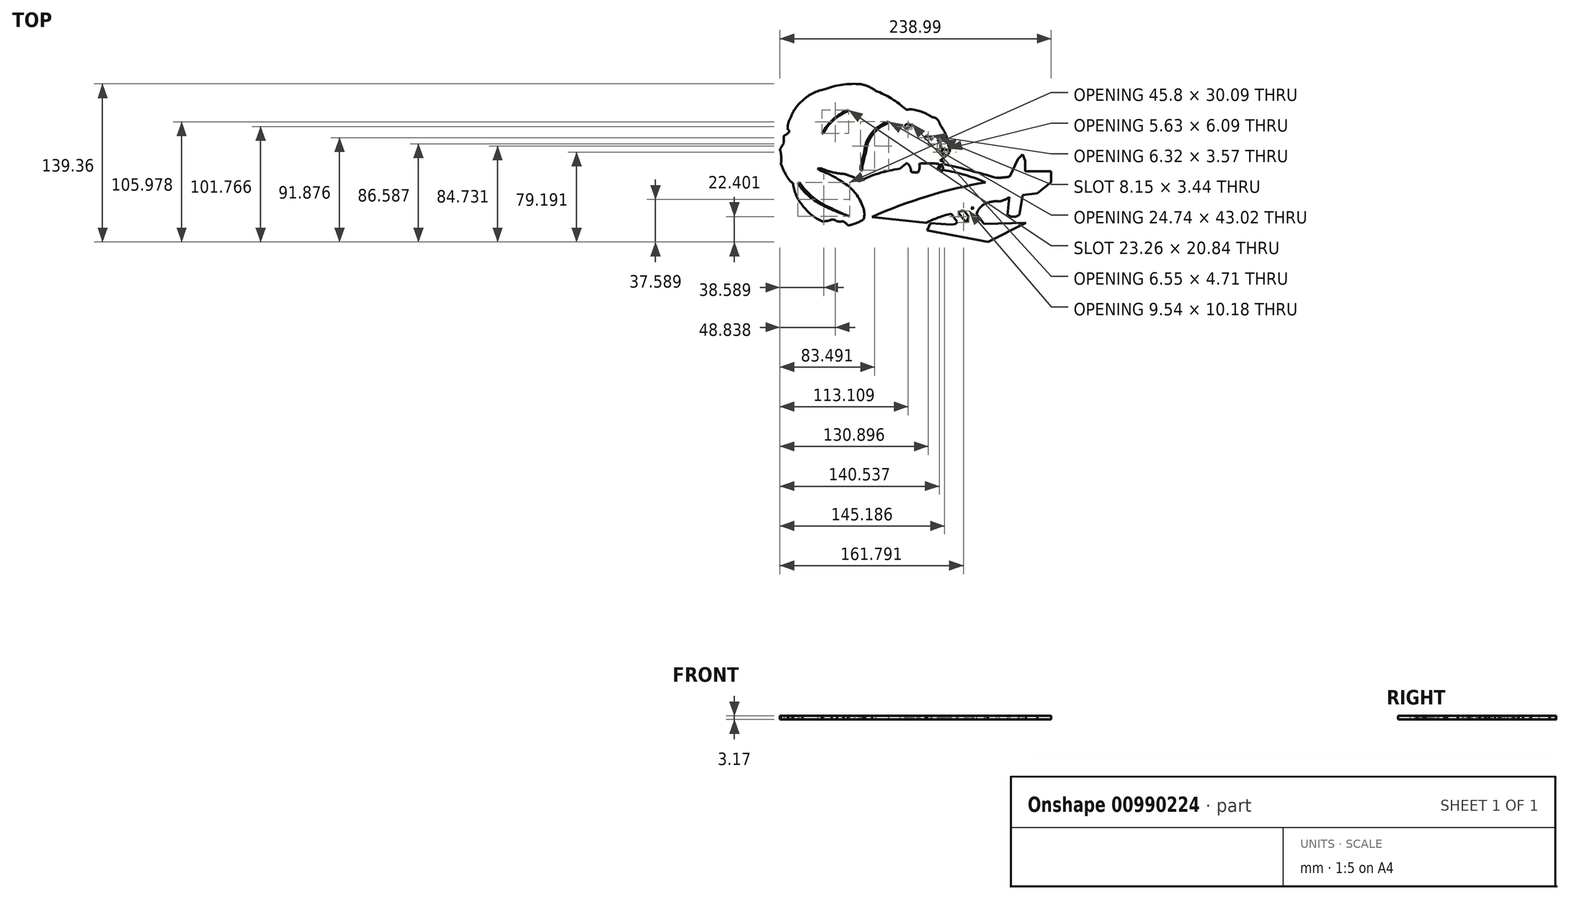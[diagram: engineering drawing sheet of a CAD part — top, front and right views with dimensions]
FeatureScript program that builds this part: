
annotation { "Feature Type Name" : "Feature", "Feature Type Description" : "" }
export const myFeature = defineFeature(function(context is Context, id is Id, definition is map)
    precondition{}
    {
        {
            var Q0;
            Q0=qCreatedBy(makeId("Top.planeOp"),FACE);
            var sketch = newSketch(context, id + "F0", { "sketchPlane" : qUnion([Q0])});
            skArc(sketch, "E0", {"start": v(160.46, 90.83) * mm, "mid": v(162.98, 93) * mm, "end": v(164.83, 95.76) * mm});
            skArc(sketch, "E1", {"start": v(164.83, 95.76) * mm, "mid": v(164.52, 98.7) * mm, "end": v(163, 101.22) * mm});
            skArc(sketch, "E2", {"start": v(163, 101.22) * mm, "mid": v(163.59, 103.27) * mm, "end": v(163, 105.33) * mm});
            skArc(sketch, "E3", {"start": v(163, 105.33) * mm, "mid": v(160.72, 111.62) * mm, "end": v(157.27, 117.36) * mm});
            skArc(sketch, "E4", {"start": v(155.17, 121.91) * mm, "mid": v(156.06, 119.56) * mm, "end": v(157.27, 117.36) * mm});
            skArc(sketch, "E5", {"start": v(155.17, 121.91) * mm, "mid": v(152.64, 124.68) * mm, "end": v(149.06, 125.83) * mm});
            skArc(sketch, "E6", {"start": v(149.06, 125.83) * mm, "mid": v(139.42, 130.68) * mm, "end": v(128.83, 132.76) * mm});
            skArc(sketch, "E7", {"start": v(126, 132.76) * mm, "mid": v(127.42, 132.3) * mm, "end": v(128.83, 132.76) * mm});
            skArc(sketch, "E8", {"start": v(126, 132.76) * mm, "mid": v(113.45, 142.03) * mm, "end": v(99.47, 148.97) * mm});
            skArc(sketch, "E9", {"start": v(99.47, 148.97) * mm, "mid": v(93.3, 152.63) * mm, "end": v(86.46, 154.73) * mm});
            skArc(sketch, "E10", {"start": v(86.46, 154.73) * mm, "mid": v(69.87, 154.35) * mm, "end": v(53.83, 150.08) * mm});
            skArc(sketch, "E11", {"start": v(53.83, 150.08) * mm, "mid": v(43.24, 146.4) * mm, "end": v(34.23, 139.7) * mm});
            skArc(sketch, "E12", {"start": v(34.23, 139.7) * mm, "mid": v(28.64, 133.35) * mm, "end": v(24.76, 125.83) * mm});
            skArc(sketch, "E13", {"start": v(24.76, 125.83) * mm, "mid": v(22.51, 120.68) * mm, "end": v(21.86, 115.1) * mm});
            skArc(sketch, "E14", {"start": v(23.32, 112.91) * mm, "mid": v(22.86, 114.18) * mm, "end": v(21.86, 115.1) * mm});
            skArc(sketch, "E15", {"start": v(18.67, 109.45) * mm, "mid": v(21.21, 110.9) * mm, "end": v(23.32, 112.91) * mm});
            skArc(sketch, "E16", {"start": v(18.67, 109.45) * mm, "mid": v(18.36, 106.3) * mm, "end": v(18.67, 103.16) * mm});
            skArc(sketch, "E17", {"start": v(18.67, 103.16) * mm, "mid": v(16.8, 100.19) * mm, "end": v(15.01, 97.17) * mm});
            skArc(sketch, "E18", {"start": v(16.05, 93.03) * mm, "mid": v(15.68, 95.14) * mm, "end": v(15.01, 97.17) * mm});
            skArc(sketch, "E19", {"start": v(16.05, 84.77) * mm, "mid": v(16.17, 88.9) * mm, "end": v(16.05, 93.03) * mm});
            skArc(sketch, "E20", {"start": v(16.05, 84.77) * mm, "mid": v(18.51, 78.47) * mm, "end": v(21.86, 72.6) * mm});
            skArc(sketch, "E21", {"start": v(21.86, 72.6) * mm, "mid": v(23.94, 69.68) * mm, "end": v(26.73, 67.43) * mm});
            skArc(sketch, "E22", {"start": v(26.73, 67.43) * mm, "mid": v(29.3, 56.97) * mm, "end": v(35.1, 47.9) * mm});
            skArc(sketch, "E23", {"start": v(35.1, 47.9) * mm, "mid": v(42.8, 39.74) * mm, "end": v(52.45, 34) * mm});
            skArc(sketch, "E24", {"start": v(74.96, 30.33) * mm, "mid": v(82.12, 32.25) * mm, "end": v(88.74, 35.62) * mm});
            skArc(sketch, "E25", {"start": v(88.74, 35.62) * mm, "mid": v(89.4, 41.86) * mm, "end": v(87.7, 47.9) * mm});
            skArc(sketch, "E26", {"start": v(87.7, 47.9) * mm, "mid": v(80.74, 59.73) * mm, "end": v(70.25, 68.58) * mm});
            skArc(sketch, "E27", {"start": v(70.25, 68.58) * mm, "mid": v(60.84, 74.2) * mm, "end": v(50.84, 78.68) * mm});
            skArc(sketch, "E28", {"start": v(48.2, 80.6) * mm, "mid": v(49.41, 79.49) * mm, "end": v(50.84, 78.68) * mm});
            skArc(sketch, "E29", {"start": v(53.83, 79.6) * mm, "mid": v(51.1, 80.62) * mm, "end": v(48.2, 80.6) * mm});
            skArc(sketch, "E30", {"start": v(53.83, 79.6) * mm, "mid": v(62.89, 76.93) * mm, "end": v(72.24, 75.62) * mm});
            skArc(sketch, "E31", {"start": v(72.24, 75.62) * mm, "mid": v(76.5, 74.1) * mm, "end": v(80.77, 72.6) * mm});
            skArc(sketch, "E32", {"start": v(126, 84.77) * mm, "mid": v(102.6, 81.62) * mm, "end": v(80.77, 72.6) * mm});
            skArc(sketch, "E33", {"start": v(153.6, 84.77) * mm, "mid": v(145.69, 85.05) * mm, "end": v(137.76, 84.77) * mm});
            skArc(sketch, "E34", {"start": v(156.02, 87.46) * mm, "mid": v(158.32, 89.04) * mm, "end": v(160.46, 90.83) * mm});
            skArc(sketch, "E35", {"start": v(160.46, 84.77) * mm, "mid": v(158.62, 86.74) * mm, "end": v(156.02, 87.46) * mm});
            skArc(sketch, "E36", {"start": v(157.83, 95.76) * mm, "mid": v(158.13, 93.86) * mm, "end": v(159.04, 92.17) * mm});
            skArc(sketch, "E37", {"start": v(161.22, 97.17) * mm, "mid": v(159.2, 97.25) * mm, "end": v(157.83, 95.76) * mm});
            skArc(sketch, "E38", {"start": v(161.22, 97.17) * mm, "mid": v(162.11, 96.82) * mm, "end": v(163, 97.17) * mm});
            skArc(sketch, "E39", {"start": v(157.27, 98.2) * mm, "mid": v(156.43, 102.55) * mm, "end": v(154.16, 106.35) * mm});
            skArc(sketch, "E40", {"start": v(131.4, 118.08) * mm, "mid": v(128.77, 116.93) * mm, "end": v(126.57, 115.1) * mm});
            skArc(sketch, "E41", {"start": v(124.85, 116.87) * mm, "mid": v(125.44, 115.73) * mm, "end": v(126.57, 115.1) * mm});
            skArc(sketch, "E42", {"start": v(128.8, 119.69) * mm, "mid": v(126.14, 119.25) * mm, "end": v(124.85, 116.87) * mm});
            skArc(sketch, "E43", {"start": v(131.4, 118.08) * mm, "mid": v(130.22, 119.08) * mm, "end": v(128.8, 119.69) * mm});
            skArc(sketch, "E44", {"start": v(149.06, 105.83) * mm, "mid": v(147.66, 108.15) * mm, "end": v(145.22, 109.33) * mm});
            skArc(sketch, "E45", {"start": v(145.22, 109.33) * mm, "mid": v(143.62, 108.94) * mm, "end": v(142.75, 107.55) * mm});
            skArc(sketch, "E46", {"start": v(110.87, 120.48) * mm, "mid": v(96.75, 110.42) * mm, "end": v(90.85, 94.1) * mm});
            skArc(sketch, "E47", {"start": v(90.85, 94.1) * mm, "mid": v(89.5, 90.08) * mm, "end": v(88.7, 85.92) * mm});
            skArc(sketch, "E48", {"start": v(75.48, 131.3) * mm, "mid": v(62.46, 123.3) * mm, "end": v(53.05, 111.25) * mm});
            skArc(sketch, "E49", {"start": v(88.7, 85.92) * mm, "mid": v(87.74, 82.48) * mm, "end": v(87.85, 78.91) * mm});
            skArc(sketch, "E50", {"start": v(120.78, 80.26) * mm, "mid": v(102.14, 76.26) * mm, "end": v(84.5, 69.05) * mm});
            skArc(sketch, "E51", {"start": v(130.6, 77.85) * mm, "mid": v(129.87, 81.62) * mm, "end": v(127.68, 84.77) * mm});
            skArc(sketch, "E52", {"start": v(133.15, 77.4) * mm, "mid": v(132.91, 80.68) * mm, "end": v(132.6, 83.96) * mm});
            skArc(sketch, "E53", {"start": v(135.6, 77.21) * mm, "mid": v(135.81, 79.9) * mm, "end": v(135.88, 82.59) * mm});
            skArc(sketch, "E54", {"start": v(136.8, 77.21) * mm, "mid": v(138.13, 80.88) * mm, "end": v(137.76, 84.77) * mm});
            skArc(sketch, "E55", {"start": v(153.6, 80.22) * mm, "mid": v(155.03, 82.27) * mm, "end": v(154.93, 84.77) * mm});
            skArc(sketch, "E56", {"start": v(154.84, 79.58) * mm, "mid": v(156.54, 81.91) * mm, "end": v(156.94, 84.77) * mm});
            skArc(sketch, "E57", {"start": v(158.49, 79.49) * mm, "mid": v(158.5, 82.36) * mm, "end": v(156.94, 84.77) * mm});
            skArc(sketch, "E58", {"start": v(156.94, 78.78) * mm, "mid": v(157.72, 79.11) * mm, "end": v(158.49, 79.49) * mm});
            skArc(sketch, "E59", {"start": v(157.68, 77.98) * mm, "mid": v(159.94, 80.65) * mm, "end": v(160.28, 84.13) * mm});
            skArc(sketch, "E60", {"start": v(160.28, 84.13) * mm, "mid": v(159.87, 85.19) * mm, "end": v(159.35, 86.2) * mm});
            skArc(sketch, "E61", {"start": v(153.6, 80.22) * mm, "mid": v(154.06, 79.6) * mm, "end": v(154.84, 79.58) * mm});
            skArc(sketch, "E62", {"start": v(135.6, 77.21) * mm, "mid": v(136.2, 76.97) * mm, "end": v(136.8, 77.21) * mm});
            skArc(sketch, "E63", {"start": v(133.15, 77.4) * mm, "mid": v(134.35, 76.94) * mm, "end": v(135.6, 77.21) * mm});
            skArc(sketch, "E64", {"start": v(130.6, 77.85) * mm, "mid": v(131.8, 77.22) * mm, "end": v(133.15, 77.4) * mm});
            skArc(sketch, "E65", {"start": v(151.46, 80.22) * mm, "mid": v(145.6, 80.37) * mm, "end": v(139.74, 80.36) * mm});
            skArc(sketch, "E66", {"start": v(153.6, 84.77) * mm, "mid": v(154.27, 84.73) * mm, "end": v(154.93, 84.77) * mm});
            skArc(sketch, "E67", {"start": v(156.94, 78.78) * mm, "mid": v(156.75, 77.86) * mm, "end": v(157.68, 77.98) * mm});
            skArc(sketch, "E68", {"start": v(127.68, 84.77) * mm, "mid": v(126.84, 84.96) * mm, "end": v(126, 84.77) * mm});
            skArc(sketch, "E69", {"start": v(32.35, 68.32) * mm, "mid": v(44.4, 54.95) * mm, "end": v(59.91, 45.81) * mm});
            skArc(sketch, "E70", {"start": v(59.91, 45.81) * mm, "mid": v(68.08, 41.75) * mm, "end": v(76.5, 38.24) * mm});
            skArc(sketch, "E71", {"start": v(30.7, 67.53) * mm, "mid": v(38.47, 58.05) * mm, "end": v(48.2, 50.58) * mm});
            skArc(sketch, "E72", {"start": v(48.2, 50.58) * mm, "mid": v(62.07, 43.77) * mm, "end": v(76.5, 38.24) * mm});
            skArc(sketch, "E73", {"start": v(74.82, 132.09) * mm, "mid": v(61.86, 123.64) * mm, "end": v(52.22, 111.54) * mm});
            skLineSegment(sketch, "E74", {"start": v(53.05, 111.25) * mm, "end": v(52.22, 111.54) * mm});
            skLineSegment(sketch, "E75", {"start": v(75.48, 131.3) * mm, "end": v(74.82, 132.09) * mm});
            skArc(sketch, "E76.0", {"start": v(87.2, 86.34) * mm, "mid": v(86.23, 82.69) * mm, "end": v(86.3, 78.91) * mm});
            skArc(sketch, "E76.1", {"start": v(89.34, 94.43) * mm, "mid": v(88.03, 90.45) * mm, "end": v(87.2, 86.34) * mm});
            skArc(sketch, "E76.2", {"start": v(110.4, 121.93) * mm, "mid": v(95.61, 111.44) * mm, "end": v(89.34, 94.43) * mm});
            skLineSegment(sketch, "E77", {"start": v(87.85, 78.91) * mm, "end": v(86.3, 78.91) * mm});
            skLineSegment(sketch, "E78", {"start": v(110.87, 120.48) * mm, "end": v(110.4, 121.93) * mm});
            skArc(sketch, "E79", {"start": v(196.37, 68.37) * mm, "mid": v(145.37, 56.17) * mm, "end": v(96.24, 37.82) * mm});
            skArc(sketch, "E80", {"start": v(196.37, 68.37) * mm, "mid": v(178.04, 74.85) * mm, "end": v(159.09, 79.24) * mm});
            skArc(sketch, "E81", {"start": v(205.68, 72.27) * mm, "mid": v(183.09, 78.62) * mm, "end": v(160.28, 84.13) * mm});
            skArc(sketch, "E82", {"start": v(205.68, 72.27) * mm, "mid": v(211.55, 72.55) * mm, "end": v(217.39, 73.3) * mm});
            skArc(sketch, "E83", {"start": v(207.86, 51.49) * mm, "mid": v(212.83, 52.81) * mm, "end": v(217.27, 55.4) * mm});
            skArc(sketch, "E84", {"start": v(207.86, 51.49) * mm, "mid": v(202.66, 51.42) * mm, "end": v(197.64, 50.1) * mm});
            skArc(sketch, "E85", {"start": v(197.64, 50.1) * mm, "mid": v(191.81, 46.35) * mm, "end": v(188.34, 40.35) * mm});
            skArc(sketch, "E86", {"start": v(197.64, 57.92) * mm, "mid": v(190.11, 52.25) * mm, "end": v(184.78, 44.48) * mm});
            skArc(sketch, "E87", {"start": v(177.43, 43.1) * mm, "mid": v(174.6, 42.99) * mm, "end": v(172.03, 41.84) * mm});
            skArc(sketch, "E88", {"start": v(166.06, 40.7) * mm, "mid": v(154.75, 37.3) * mm, "end": v(143.9, 32.65) * mm});
            skLineSegment(sketch, "E89", {"start": v(217.39, 73.3) * mm, "end": v(224.74, 88.92) * mm});
            skLineSegment(sketch, "E90", {"start": v(224.74, 88.92) * mm, "end": v(228.87, 92.83) * mm});
            skLineSegment(sketch, "E91", {"start": v(228.87, 92.83) * mm, "end": v(231.17, 87.32) * mm});
            skLineSegment(sketch, "E92", {"start": v(231.17, 87.32) * mm, "end": v(231.17, 78.13) * mm});
            skLineSegment(sketch, "E93", {"start": v(231.17, 78.13) * mm, "end": v(235.3, 78.13) * mm});
            skLineSegment(sketch, "E94", {"start": v(235.3, 78.13) * mm, "end": v(254, 78.13) * mm});
            skLineSegment(sketch, "E95", {"start": v(254, 78.13) * mm, "end": v(254, 68.48) * mm});
            skLineSegment(sketch, "E96", {"start": v(254, 68.48) * mm, "end": v(241.96, 58.84) * mm});
            skLineSegment(sketch, "E97", {"start": v(241.96, 58.84) * mm, "end": v(228.87, 57) * mm});
            skLineSegment(sketch, "E98", {"start": v(228.87, 57) * mm, "end": v(226.12, 39.77) * mm});
            skArc(sketch, "E99", {"start": v(215.55, 39.77) * mm, "mid": v(220.83, 37.92) * mm, "end": v(226.12, 39.77) * mm});
            skLineSegment(sketch, "E100", {"start": v(215.55, 39.77) * mm, "end": v(217.27, 55.4) * mm});
            skLineSegment(sketch, "E101", {"start": v(177.43, 43.1) * mm, "end": v(181.57, 37.64) * mm});
            skLineSegment(sketch, "E102", {"start": v(181.57, 37.64) * mm, "end": v(180.2, 35.63) * mm});
            skLineSegment(sketch, "E103", {"start": v(180.2, 35.63) * mm, "end": v(180.2, 33.63) * mm});
            skLineSegment(sketch, "E104", {"start": v(180.2, 33.63) * mm, "end": v(179.13, 33) * mm});
            skLineSegment(sketch, "E105", {"start": v(179.13, 33) * mm, "end": v(172.03, 41.84) * mm});
            skLineSegment(sketch, "E106", {"start": v(166.06, 40.7) * mm, "end": v(171.18, 33.54) * mm});
            skLineSegment(sketch, "E107", {"start": v(171.18, 33.54) * mm, "end": v(170.36, 31.62) * mm});
            skLineSegment(sketch, "E108", {"start": v(170.36, 31.62) * mm, "end": v(166.06, 31.1) * mm});
            skLineSegment(sketch, "E109", {"start": v(166.06, 31.1) * mm, "end": v(143.9, 32.65) * mm});
            skArc(sketch, "E110", {"start": v(52.45, 34) * mm, "mid": v(56.58, 34.3) * mm, "end": v(60.59, 35.37) * mm});
            skArc(sketch, "E111", {"start": v(65.42, 34) * mm, "mid": v(63.13, 35.15) * mm, "end": v(60.59, 35.37) * mm});
            skArc(sketch, "E112", {"start": v(65.42, 34) * mm, "mid": v(68.06, 33.73) * mm, "end": v(70.7, 34) * mm});
            skArc(sketch, "E113", {"start": v(74.96, 30.33) * mm, "mid": v(73.05, 32.43) * mm, "end": v(70.7, 34) * mm});
            skLineSegment(sketch, "E114", {"start": v(30.7, 67.53) * mm, "end": v(32.35, 68.32) * mm});
            skArc(sketch, "E115", {"start": v(157.38, 95.78) * mm, "mid": v(157.79, 93.73) * mm, "end": v(158.68, 91.84) * mm});
            skArc(sketch, "E116", {"start": v(161.25, 97.66) * mm, "mid": v(158.87, 97.65) * mm, "end": v(157.38, 95.78) * mm});
            skArc(sketch, "E117", {"start": v(161.25, 97.66) * mm, "mid": v(162, 97.18) * mm, "end": v(162.84, 97.47) * mm});
            skLineSegment(sketch, "E118", {"start": v(159.04, 92.17) * mm, "end": v(158.68, 91.84) * mm});
            skLineSegment(sketch, "E119", {"start": v(163, 97.17) * mm, "end": v(162.84, 97.47) * mm});
            skArc(sketch, "E120", {"start": v(156.74, 98.2) * mm, "mid": v(156.03, 102.4) * mm, "end": v(153.83, 106.03) * mm});
            skArc(sketch, "E121", {"start": v(148.66, 105.78) * mm, "mid": v(147.4, 107.88) * mm, "end": v(145.21, 108.97) * mm});
            skArc(sketch, "E122", {"start": v(145.21, 108.97) * mm, "mid": v(143.82, 108.64) * mm, "end": v(143.1, 107.4) * mm});
            skLineSegment(sketch, "E123", {"start": v(143.1, 107.4) * mm, "end": v(142.75, 107.55) * mm});
            skLineSegment(sketch, "E124", {"start": v(149.06, 105.83) * mm, "end": v(148.66, 105.78) * mm});
            skLineSegment(sketch, "E125", {"start": v(154.16, 106.35) * mm, "end": v(153.83, 106.03) * mm});
            skLineSegment(sketch, "E126", {"start": v(157.27, 98.2) * mm, "end": v(156.74, 98.2) * mm});
            skLineSegment(sketch, "E127", {"start": v(96.24, 37.82) * mm, "end": v(143.9, 32.65) * mm});
            skLineSegment(sketch, "E128", {"start": v(166.06, 40.7) * mm, "end": v(164.26, 44.13) * mm});
            skLineSegment(sketch, "E129", {"start": v(164.26, 44.13) * mm, "end": v(163.98, 48.51) * mm});
            skLineSegment(sketch, "E130", {"start": v(163.98, 48.51) * mm, "end": v(166.06, 48.25) * mm});
            skLineSegment(sketch, "E131", {"start": v(166.06, 48.25) * mm, "end": v(172.03, 41.84) * mm});
            skLineSegment(sketch, "E132", {"start": v(177.43, 43.1) * mm, "end": v(169.14, 52.13) * mm});
            skLineSegment(sketch, "E133", {"start": v(169.14, 52.13) * mm, "end": v(167.65, 60.3) * mm});
            skLineSegment(sketch, "E134", {"start": v(167.65, 60.3) * mm, "end": v(168.86, 60.7) * mm});
            skLineSegment(sketch, "E135", {"start": v(168.86, 60.7) * mm, "end": v(176.5, 53.5) * mm});
            skLineSegment(sketch, "E136", {"start": v(176.5, 53.5) * mm, "end": v(184.78, 44.48) * mm});
            skLineSegment(sketch, "E137", {"start": v(84.5, 69.05) * mm, "end": v(80.77, 72.6) * mm});
            skLineSegment(sketch, "E138", {"start": v(120.78, 80.26) * mm, "end": v(126, 84.77) * mm});
            skLineSegment(sketch, "E139", {"start": v(147.64, 32.4) * mm, "end": v(144.77, 26.14) * mm});
            skLineSegment(sketch, "E140", {"start": v(144.77, 26.14) * mm, "end": v(198.63, 15.69) * mm});
            skLineSegment(sketch, "E141", {"start": v(198.63, 15.69) * mm, "end": v(231.93, 32.65) * mm});
            skLineSegment(sketch, "E142", {"start": v(231.93, 32.65) * mm, "end": v(194.85, 31.8) * mm});
            skLineSegment(sketch, "E143", {"start": v(194.85, 31.8) * mm, "end": v(188.34, 40.35) * mm});
            skLineSegment(sketch, "E144", {"start": v(183.5, 45.87) * mm, "end": v(185.68, 46.25) * mm});
            skSolve(sketch);
        }
        {
            var Q0;
            Q0=makeQuery(id+"F0.imprint","IMPRINT",FACE,{"disambiguationData":[TD([[makeQuery(id+"F0.imprint","IMPRINT",EDGE,{"derivedFrom":sQuery(id+"F0.wireOp",EDGE,"E0")}),1.0]])]});
            var Q1;
            Q1=makeQuery(id+"F0.imprint","IMPRINT",FACE,{"disambiguationData":[TD([[makeQuery(id+"F0.imprint","IMPRINT",EDGE,{"derivedFrom":sQuery(id+"F0.wireOp",EDGE,"E79")}),1.0]])]});
            var Q2;
            Q2=makeQuery(id+"F0.imprint","IMPRINT",FACE,{"disambiguationData":[TD([[makeQuery(id+"F0.imprint","IMPRINT",EDGE,{"derivedFrom":sQuery(id+"F0.wireOp",EDGE,"E32")}),1.0]])]});
            extrude(context, id + "F1", {"entities" : qUnion([Q0, Q1, Q2]), "depth" : 3.17 * mm, "offsetDistance" : 25.4 * mm});
        }
    });
